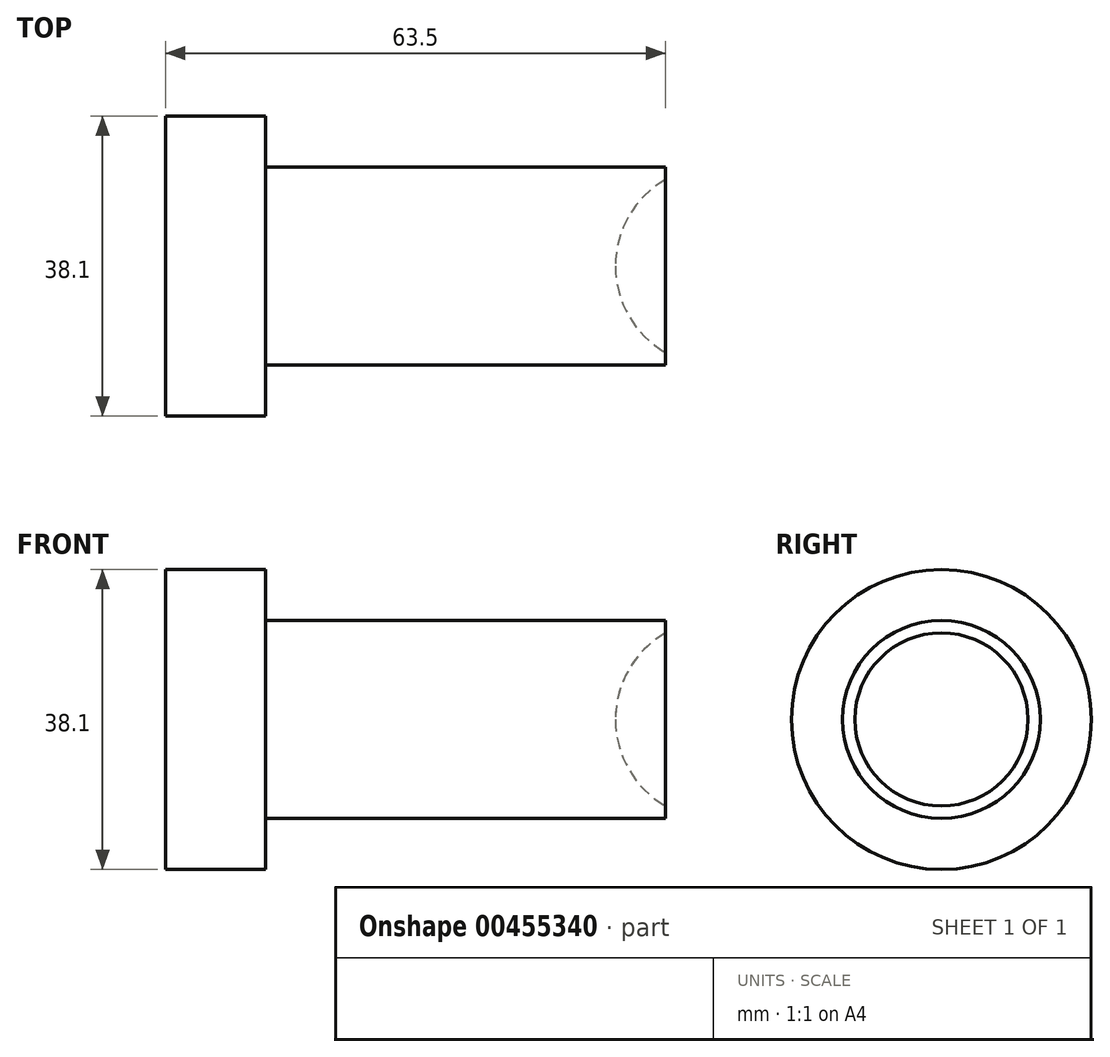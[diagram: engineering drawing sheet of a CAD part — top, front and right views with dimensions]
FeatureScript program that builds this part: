
annotation { "Feature Type Name" : "Feature", "Feature Type Description" : "" }
export const myFeature = defineFeature(function(context is Context, id is Id, definition is map)
    precondition{}
    {
        {
            var Q0;
            Q0=qCreatedBy(makeId("Front.planeOp"),FACE);
            var sketch = newSketch(context, id + "F0", { "sketchPlane" : qUnion([Q0])});
            skLineSegment(sketch, "E0", {"start": v(-34.66, 0) * mm, "end": v(-34.66, 19.05) * mm});
            skLineSegment(sketch, "E1", {"start": v(-34.66, 19.05) * mm, "end": v(-21.96, 19.05) * mm});
            skLineSegment(sketch, "E2", {"start": v(-21.96, 19.05) * mm, "end": v(-21.96, 12.57) * mm});
            skLineSegment(sketch, "E3", {"start": v(-21.96, 12.57) * mm, "end": v(28.84, 12.57) * mm});
            skLineSegment(sketch, "E4", {"start": v(28.84, 12.57) * mm, "end": v(28.84, 11) * mm});
            skLineSegment(sketch, "E5", {"start": v(28.84, 0) * mm, "end": v(-34.66, 0) * mm});
            skLineSegment(sketch, "E6", {"start": v(35.2, -5.57) * mm, "end": v(35.2, 5.57) * mm});
            skArc(sketch, "E7", {"start": v(28.84, 11) * mm, "mid": v(24.2, 6.35) * mm, "end": v(22.5, 0) * mm});
            skLineSegment(sketch, "E8", {"start": v(-65.63, 0) * mm, "end": v(53.93, 0) * mm});
            skSolve(sketch);
        }
        {
            var Q0;
            {var subQ0=sQuery(id+"F0.wireOp",EDGE,"E0");Q0=makeQuery(id+"F0.imprint","IMPRINT",FACE,{"disambiguationData":[TD([[makeQuery(id+"F0.imprint","IMPRINT",EDGE,{"derivedFrom":subQ0}),-1.0]])]});}
            var Q1;
            Q1=sQuery(id+"F0.wireOp",EDGE,"E8");
            revolve(context, id + "F1", {"entities" : qUnion([Q0]), "axis" : qUnion([Q1]), "revolveType" : RevolveType.FULL});
        }
    });
